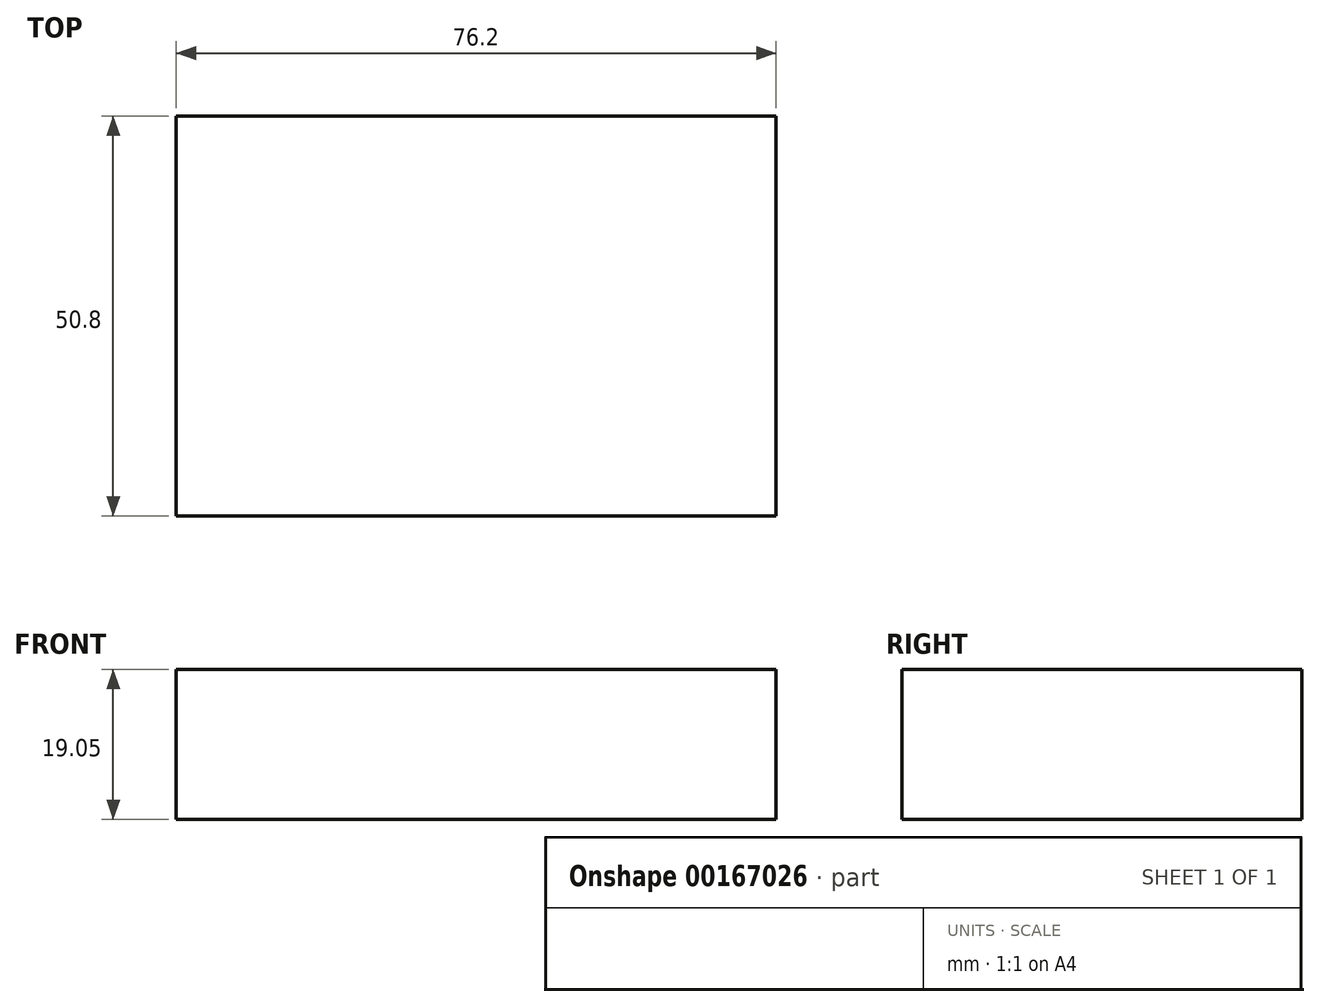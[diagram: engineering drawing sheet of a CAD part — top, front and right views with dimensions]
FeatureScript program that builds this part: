
annotation { "Feature Type Name" : "Feature", "Feature Type Description" : "" }
export const myFeature = defineFeature(function(context is Context, id is Id, definition is map)
    precondition{}
    {
        {
            var Q0;
            Q0=qCreatedBy(makeId("Top.planeOp"),FACE);
            var sketch = newSketch(context, id + "F0", { "sketchPlane" : qUnion([Q0])});
            skLineSegment(sketch, "E0.bottom", {"start": v(-43.74, 0) * mm, "end": v(32.46, 0) * mm});
            skLineSegment(sketch, "E0.top", {"start": v(-43.74, 50.8) * mm, "end": v(32.46, 50.8) * mm});
            skLineSegment(sketch, "E0.left", {"start": v(-43.74, 0) * mm, "end": v(-43.74, 50.8) * mm});
            skLineSegment(sketch, "E0.right", {"start": v(32.46, 0) * mm, "end": v(32.46, 50.8) * mm});
            skSolve(sketch);
        }
        {
            var Q0;
            Q0=makeQuery(id+"F0.imprint","IMPRINT",FACE,{"disambiguationData":[TD([[makeQuery(id+"F0.imprint","IMPRINT",EDGE,{"derivedFrom":sQuery(id+"F0.wireOp",EDGE,"E0.bottom")}),1.0]])]});
            extrude(context, id + "F1", {"entities" : qUnion([Q0]), "depth" : 19.05 * mm});
        }
    });
